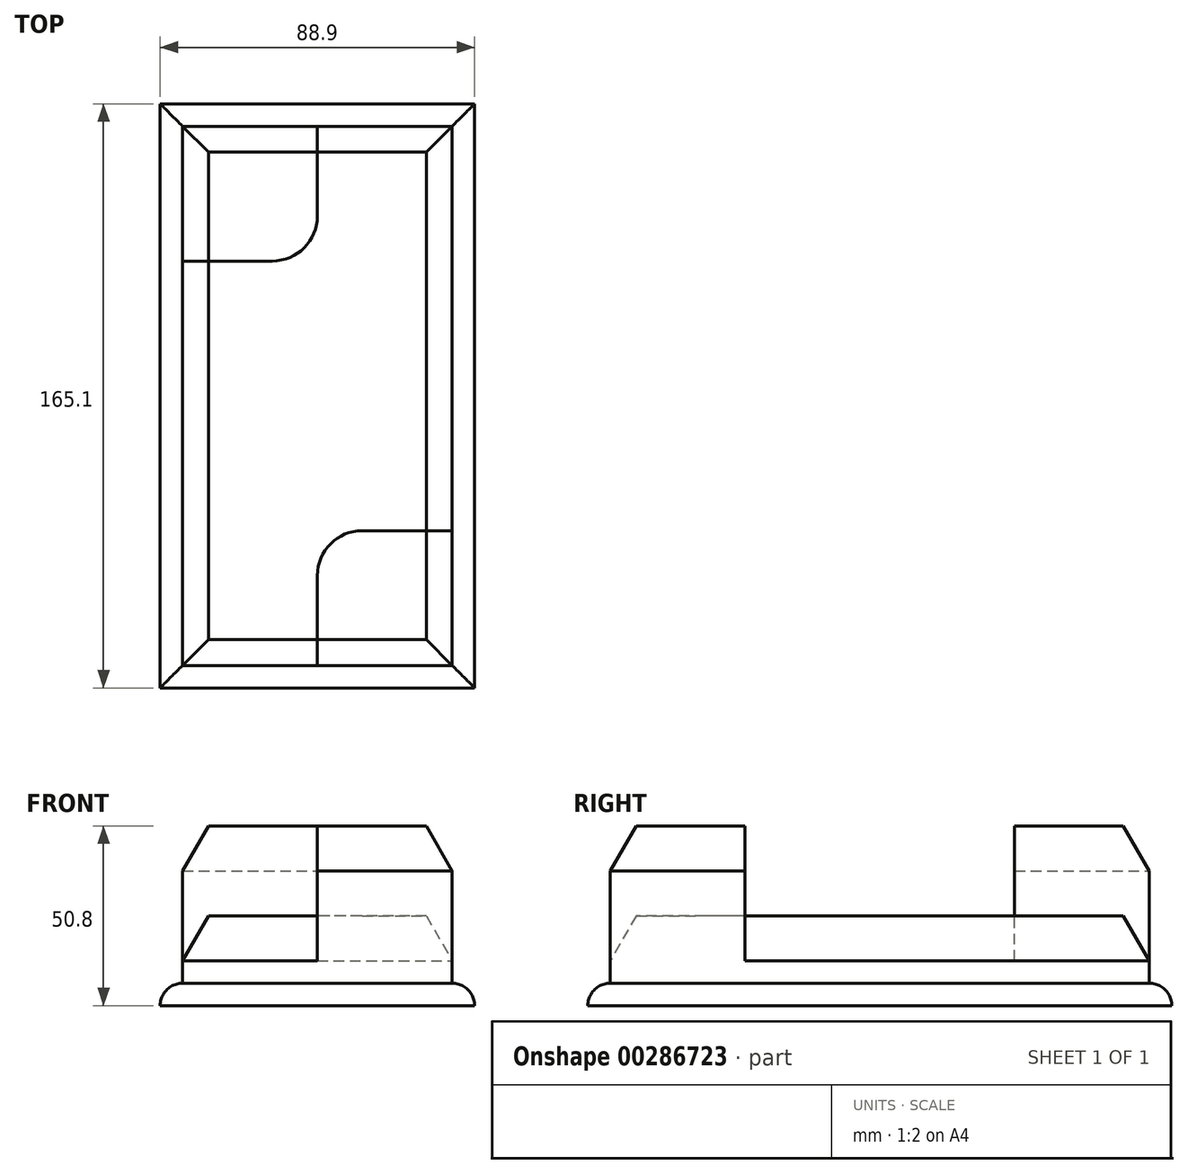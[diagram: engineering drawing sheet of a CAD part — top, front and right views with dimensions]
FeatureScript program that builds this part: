
annotation { "Feature Type Name" : "Feature", "Feature Type Description" : "" }
export const myFeature = defineFeature(function(context is Context, id is Id, definition is map)
    precondition{}
    {
        {
            var Q0;
            Q0=qCreatedBy(makeId("Top.planeOp"),FACE);
            var sketch = newSketch(context, id + "F0", { "sketchPlane" : qUnion([Q0])});
            skLineSegment(sketch, "E0.bottom", {"start": v(-38.1, 76.2) * mm, "end": v(38.1, 76.2) * mm});
            skLineSegment(sketch, "E0.top", {"start": v(-38.1, -76.2) * mm, "end": v(38.1, -76.2) * mm});
            skLineSegment(sketch, "E0.left", {"start": v(-38.1, 76.2) * mm, "end": v(-38.1, -76.2) * mm});
            skLineSegment(sketch, "E0.right", {"start": v(38.1, 76.2) * mm, "end": v(38.1, -76.2) * mm});
            skLineSegment(sketch, "E1.0", {"start": v(-44.45, 82.55) * mm, "end": v(44.45, 82.55) * mm});
            skLineSegment(sketch, "E1.1", {"start": v(-44.45, 82.55) * mm, "end": v(-44.45, -82.55) * mm});
            skLineSegment(sketch, "E1.2", {"start": v(-44.45, -82.55) * mm, "end": v(44.45, -82.55) * mm});
            skLineSegment(sketch, "E1.3", {"start": v(44.45, 82.55) * mm, "end": v(44.45, -82.55) * mm});
            skPoint(sketch, "E2", {"position": v(0, 76.2) * mm});
            skLineSegment(sketch, "E3", {"start": v(0, 76.2) * mm, "end": v(0, 50.8) * mm});
            skLineSegment(sketch, "E4", {"start": v(-38.1, 38.1) * mm, "end": v(-12.7, 38.1) * mm});
            skPoint(sketch, "E5.visualSharp", {"position": v(0, 38.1) * mm});
            skArc(sketch, "E5.filletArc", {"start": v(-12.7, 38.1) * mm, "mid": v(-3.72, 41.82) * mm, "end": v(0, 50.8) * mm});
            skPoint(sketch, "E6", {"position": v(0, -76.2) * mm});
            skLineSegment(sketch, "E7", {"start": v(0, -76.2) * mm, "end": v(0, -50.8) * mm});
            skLineSegment(sketch, "E8", {"start": v(12.7, -38.1) * mm, "end": v(38.1, -38.1) * mm});
            skPoint(sketch, "E9.visualSharp", {"position": v(0, -38.1) * mm});
            skArc(sketch, "E9.filletArc", {"start": v(12.7, -38.1) * mm, "mid": v(3.72, -41.82) * mm, "end": v(0, -50.8) * mm});
            skSolve(sketch);
        }
        {
            var Q0;
            Q0=makeQuery(id+"F0.imprint","IMPRINT",FACE,{"disambiguationData":[TD([[makeQuery(id+"F0.imprint","IMPRINT",EDGE,{"derivedFrom":sQuery(id+"F0.wireOp",EDGE,"E1.0")}),-1.0]])]});
            extrude(context, id + "F1", {"entities" : qUnion([Q0]), "depth" : 6.35 * mm});
        }
        {
            var Q0;
            {var subQ9=sQuery(id+"F0.wireOp",EDGE,"E3");Q0=makeQuery(id+"F0.imprint","IMPRINT",FACE,{"disambiguationData":[TD([[makeQuery(id+"F0.imprint","IMPRINT",EDGE,{"derivedFrom":subQ9}),1.0]])]});}
            extrude(context, id + "F2", {"entities" : qUnion([Q0]), "operationType" : NewBodyOperationType.ADD, "depth" : 25.4 * mm});
        }
        {
            var Q0;
            {var subQ1=sQuery(id+"F0.wireOp",EDGE,"E3");Q0=makeQuery(id+"F0.imprint","IMPRINT",FACE,{"disambiguationData":[TD([[makeQuery(id+"F0.imprint","IMPRINT",EDGE,{"derivedFrom":subQ1}),-1.0]])]});}
            var Q1;
            {var subQ1=sQuery(id+"F0.wireOp",EDGE,"E7");Q1=makeQuery(id+"F0.imprint","IMPRINT",FACE,{"disambiguationData":[TD([[makeQuery(id+"F0.imprint","IMPRINT",EDGE,{"derivedFrom":subQ1}),-1.0]])]});}
            extrude(context, id + "F3", {"entities" : qUnion([Q0, Q1]), "operationType" : NewBodyOperationType.ADD, "depth" : 50.8 * mm});
        }
        {
            var Q0;
            Q0=makeQuery(id+"F3.opExtrude","CAP_EDGE",EDGE,{"disambiguationData":[OSD([sQuery(id+"F0.wireOp",EDGE,"E0.top")])],"isStart":false});
            var Q1;
            Q1=makeQuery(id+"F3.opExtrude","CAP_EDGE",EDGE,{"disambiguationData":[OSD([sQuery(id+"F0.wireOp",EDGE,"E0.right")])],"isStart":false});
            var Q2;
            Q2=makeQuery(id+"F2.opExtrude","CAP_EDGE",EDGE,{"disambiguationData":[OSD([sQuery(id+"F0.wireOp",EDGE,"E0.top")])],"isStart":false});
            var Q3;
            Q3=makeQuery(id+"F2.opExtrude","CAP_EDGE",EDGE,{"disambiguationData":[OSD([sQuery(id+"F0.wireOp",EDGE,"E0.left")])],"isStart":false});
            var Q4;
            Q4=makeQuery(id+"F3.opExtrude","CAP_EDGE",EDGE,{"disambiguationData":[OSD([sQuery(id+"F0.wireOp",EDGE,"E0.left")])],"isStart":false});
            chamfer(context, id + "F4", {"entities" : qUnion([Q0, Q1, Q2, Q3, Q4]), "chamferType" : ChamferType.OFFSET_ANGLE, "width" : 12.7 * mm, "oppositeDirection" : true, "angle" : 30 * degree, "tangentPropagation" : true});
        }
        {
            var Q0;
            Q0=makeQuery(id+"F2.opExtrude","CAP_EDGE",EDGE,{"disambiguationData":[OSD([sQuery(id+"F0.wireOp",EDGE,"E0.right")])],"isStart":false});
            var Q1;
            Q1=makeQuery(id+"F2.opExtrude","CAP_EDGE",EDGE,{"disambiguationData":[OSD([sQuery(id+"F0.wireOp",EDGE,"E0.bottom")])],"isStart":false});
            var Q2;
            Q2=makeQuery(id+"F3.opExtrude","CAP_EDGE",EDGE,{"disambiguationData":[OSD([sQuery(id+"F0.wireOp",EDGE,"E0.bottom")])],"isStart":false});
            chamfer(context, id + "F5", {"entities" : qUnion([Q0, Q1, Q2]), "chamferType" : ChamferType.OFFSET_ANGLE, "width" : 12.7 * mm, "oppositeDirection" : false, "angle" : 30 * degree, "tangentPropagation" : true});
        }
        {
            var Q0;
            Q0=makeQuery(id+"F1.opExtrude","CAP_EDGE",EDGE,{"disambiguationData":[OSD([sQuery(id+"F0.wireOp",EDGE,"E1.3")])],"isStart":false});
            var Q1;
            Q1=makeQuery(id+"F1.opExtrude","CAP_EDGE",EDGE,{"disambiguationData":[OSD([sQuery(id+"F0.wireOp",EDGE,"E1.2")])],"isStart":false});
            var Q2;
            Q2=makeQuery(id+"F1.opExtrude","CAP_EDGE",EDGE,{"disambiguationData":[OSD([sQuery(id+"F0.wireOp",EDGE,"E1.1")])],"isStart":false});
            var Q3;
            Q3=makeQuery(id+"F1.opExtrude","CAP_EDGE",EDGE,{"disambiguationData":[OSD([sQuery(id+"F0.wireOp",EDGE,"E1.0")])],"isStart":false});
            fillet(context, id + "F6", {"entities" : qUnion([Q0, Q1, Q2, Q3]), "radius" : 6.35 * mm, "tangentPropagation" : true, "allowEdgeOverflow" : false});
        }
    });
